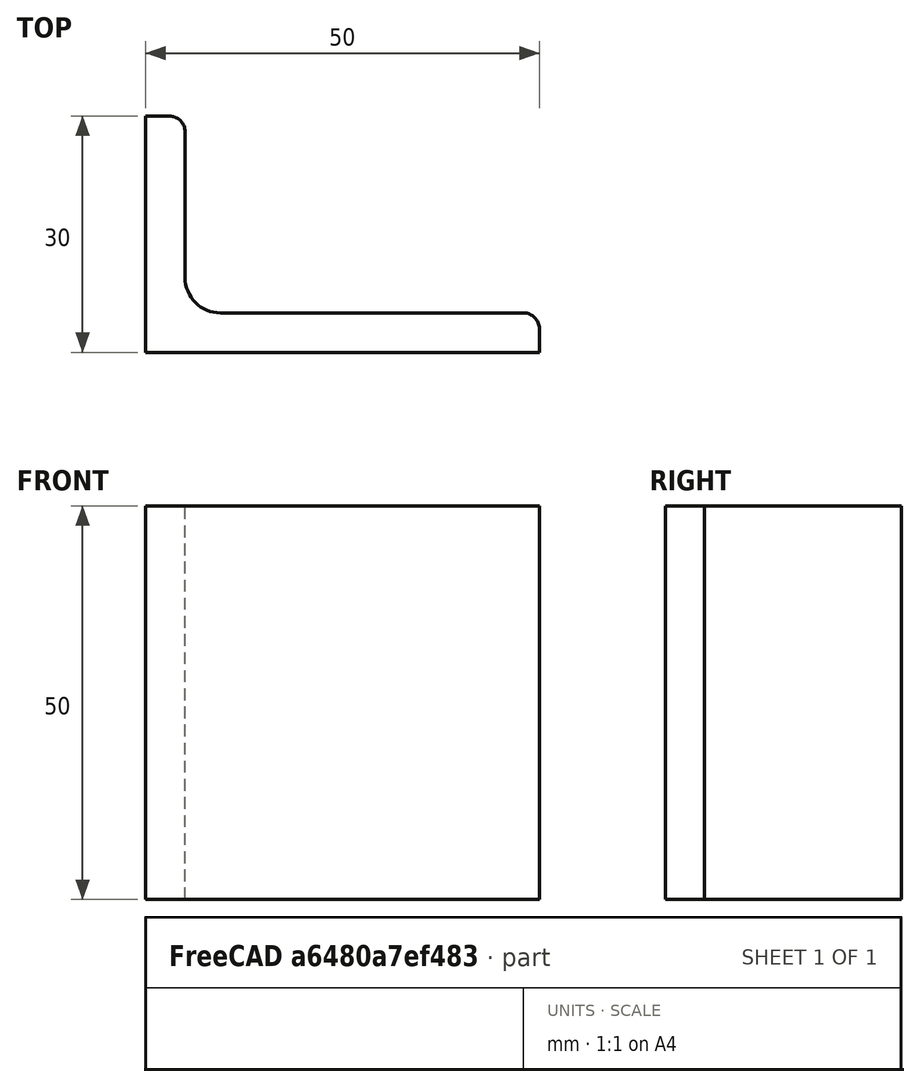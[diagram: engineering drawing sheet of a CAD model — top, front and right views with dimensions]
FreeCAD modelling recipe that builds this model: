
FCSTD DOCUMENT  (FreeCAD 0.15R4671 (Git))
Label: Angle Bar 50x30x5 EN10056 S235JR
License: All rights reserved
LicenseURL: http://en.wikipedia.org/wiki/All_rights_reserved
objects: Sketcher::SketchObject×1, Part::Extrusion×1
note: 2 computed .brp shape members not serialized (recipe doc carries the construction recipe); baked Part::Feature solids carry a one-line shape summary decoded from their .brp

FEATURE [Sketcher::SketchObject] Sketch
  sketch-geometry (9):
    g0: LineSegment StartX=0 StartY=0 StartZ=0 EndX=50 EndY=0 EndZ=0
    g1: LineSegment StartX=50 StartY=0 StartZ=0 EndX=50 EndY=3 EndZ=0
    g2: LineSegment StartX=48 StartY=5 StartZ=0 EndX=9.5 EndY=5 EndZ=0
    g3: LineSegment StartX=0 StartY=0 StartZ=0 EndX=0 EndY=30 EndZ=0
    g4: LineSegment StartX=0 StartY=30 StartZ=0 EndX=3 EndY=30 EndZ=0
    g5: LineSegment StartX=5 StartY=28 StartZ=0 EndX=5 EndY=9.5 EndZ=0
    g6: ArcOfCircle CenterX=9.5 CenterY=9.5 CenterZ=0 NormalX=0 NormalY=0 NormalZ=1 Radius=4.5 StartAngle=3.14159 EndAngle=4.71239
    g7: ArcOfCircle CenterX=3 CenterY=28 CenterZ=0 NormalX=0 NormalY=0 NormalZ=1 Radius=2 StartAngle=0 EndAngle=1.5708
    g8: ArcOfCircle CenterX=48 CenterY=3 CenterZ=0 NormalX=0 NormalY=0 NormalZ=1 Radius=2 StartAngle=0 EndAngle=1.5708
  constraints (23):
    c: Coincident(g0,g-1)
    c: Horizontal(g0)
    c: Coincident(g1,g0)
    c: Vertical(g1)
    c: Horizontal(g2)
    c: Coincident(g3,g-1)
    c: Vertical(g3)
    c: Coincident(g4,g3)
    c: Horizontal(g4)
    c: Vertical(g5)
    c: Tangent(g5,g6) = -1.5708
    c: Tangent(g2,g6) = 1.5708
    c: Tangent(g4,g7) = 1.5708
    c: Tangent(g5,g7) = 1.5708
    c: Tangent(g2,g8) = -1.5708
    c: Tangent(g1,g8) = -1.5708
    c: DistanceX(g0) = 50
    c: DistanceY(g3) = 30
    c: DistanceY(g0,g2) = 5
    c: DistanceX(g3,g5) = 5
    c: Radius(g6) = 4.5
    c: Radius(g8) = 2
    c: Radius(g7) = 2
FEATURE [Part::Extrusion] Extrude  label="Angle Bar 50x30x5 EN10056 S235JR"
  Base = -> Sketch
  Dir = (0,0,50)
  Solid = true
